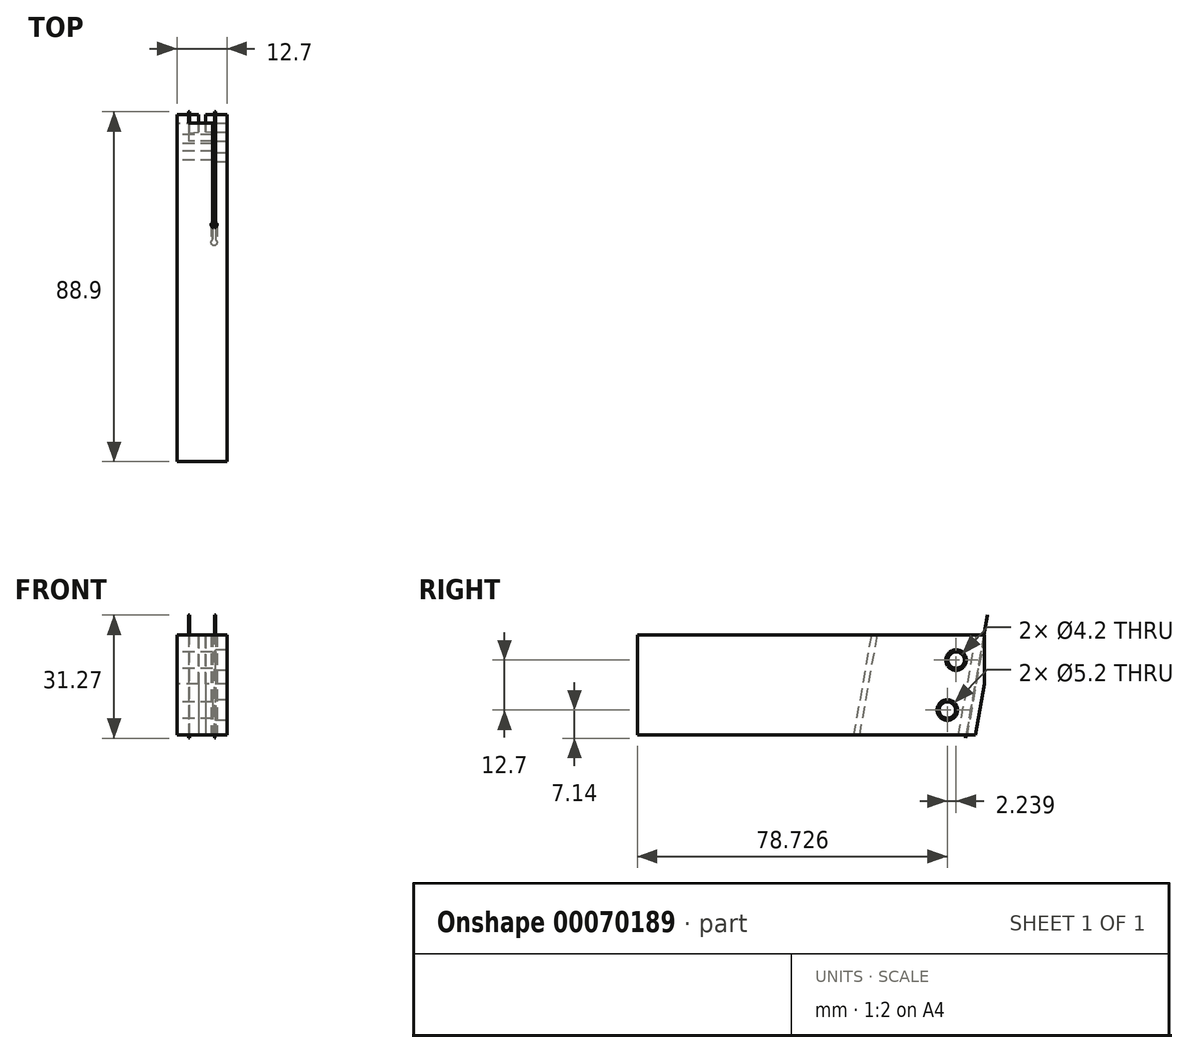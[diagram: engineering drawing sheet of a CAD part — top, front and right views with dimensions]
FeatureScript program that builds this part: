
annotation { "Feature Type Name" : "Feature", "Feature Type Description" : "" }
export const myFeature = defineFeature(function(context is Context, id is Id, definition is map)
    precondition{}
    {
        {
            var Q0;
            Q0=qCreatedBy(makeId("Right.planeOp"),FACE);
            var sketch = newSketch(context, id + "F0", { "sketchPlane" : qUnion([Q0])});
            skLineSegment(sketch, "E0", {"start": v(12.7, 0) * mm, "end": v(7.19, -31.27) * mm});
            skLineSegment(sketch, "E1", {"start": v(7.19, -31.27) * mm, "end": v(5.2, -30.92) * mm});
            skLineSegment(sketch, "E2", {"start": v(5.2, -30.92) * mm, "end": v(9.75, -5.11) * mm});
            skLineSegment(sketch, "E3", {"start": v(9.75, -5.11) * mm, "end": v(12.7, 0) * mm});
            skLineSegment(sketch, "E4", {"start": v(11.94, -17.49) * mm, "end": v(9.65, -30.48) * mm});
            skLineSegment(sketch, "E5", {"start": v(9.65, -30.48) * mm, "end": v(-76.2, -30.48) * mm});
            skLineSegment(sketch, "E6", {"start": v(-76.2, -30.48) * mm, "end": v(-76.2, -5.08) * mm});
            skLineSegment(sketch, "E7", {"start": v(-76.2, -5.08) * mm, "end": v(11.94, -5.08) * mm});
            skLineSegment(sketch, "E8", {"start": v(11.94, -5.08) * mm, "end": v(11.94, -17.49) * mm});
            skLineSegment(sketch, "E9", {"start": v(5.89, -5.08) * mm, "end": v(1.4, -30.48) * mm, "construction": true});
            skPoint(sketch, "E10", {"position": v(4.77, -11.43) * mm});
            skPoint(sketch, "E11", {"position": v(2.53, -24.13) * mm});
            skCircle(sketch, "E12", {"center": v(4.77, -11.43) * mm, "radius": 2.1 * mm});
            skCircle(sketch, "E13", {"center": v(4.77, -11.43) * mm, "radius": 2.6 * mm});
            skCircle(sketch, "E14", {"center": v(2.53, -24.13) * mm, "radius": 2.6 * mm});
            skCircle(sketch, "E15", {"center": v(2.53, -24.13) * mm, "radius": 2.1 * mm});
            skSolve(sketch);
        }
        {
            var Q0;
            {var subQ0=sQuery(id+"F0.wireOp",EDGE,"E3");Q0=makeQuery(id+"F0.imprint","IMPRINT",FACE,{"disambiguationData":[TD([[makeQuery(id+"F0.imprint","IMPRINT",EDGE,{"derivedFrom":subQ0}),-1.0]])]});}
            var Q1;
            {var subQ0=sQuery(id+"F0.wireOp",EDGE,"E1");Q1=makeQuery(id+"F0.imprint","IMPRINT",FACE,{"disambiguationData":[TD([[makeQuery(id+"F0.imprint","IMPRINT",EDGE,{"derivedFrom":subQ0}),-1.0]])]});}
            var Q2;
            {var subQ1=sQuery(id+"F0.wireOp",EDGE,"E0");var subQ7=sQuery(id+"F0.wireOp",EDGE,"E7");var subQ9=makeQuery(id+"F0.imprint","INTERSECT",VERTEX,{"derivedFrom":[subQ1,subQ7]});Q2=makeQuery(id+"F0.imprint","IMPRINT",FACE,{"disambiguationData":[TD([[makeQuery(id+"F0.imprint","IMPRINT",EDGE,{"disambiguationData":[TD([[subQ9,-1.0]])],"derivedFrom":subQ1}),-1.0]])]});}
            extrude(context, id + "F1", {"entities" : qUnion([Q0, Q1, Q2]), "depth" : 6.9 * mm});
        }
        {
            var Q0;
            {var subQ5=sQuery(id+"F0.wireOp",EDGE,"E4");Q0=makeQuery(id+"F0.imprint","IMPRINT",FACE,{"disambiguationData":[TD([[makeQuery(id+"F0.imprint","IMPRINT",EDGE,{"derivedFrom":subQ5}),-1.0]])]});}
            var Q1;
            {var subQ1=sQuery(id+"F0.wireOp",EDGE,"E0");var subQ7=sQuery(id+"F0.wireOp",EDGE,"E7");var subQ9=makeQuery(id+"F0.imprint","INTERSECT",VERTEX,{"derivedFrom":[subQ1,subQ7]});Q1=makeQuery(id+"F0.imprint","IMPRINT",FACE,{"disambiguationData":[TD([[makeQuery(id+"F0.imprint","IMPRINT",EDGE,{"disambiguationData":[TD([[subQ9,-1.0]])],"derivedFrom":subQ1}),-1.0]])]});}
            var Q2;
            {var subQ0=sQuery(id+"F0.wireOp",EDGE,"E6");Q2=makeQuery(id+"F0.imprint","IMPRINT",FACE,{"disambiguationData":[TD([[makeQuery(id+"F0.imprint","IMPRINT",EDGE,{"derivedFrom":subQ0}),-1.0]])]});}
            var Q3;
            Q3=makeQuery(id+"F0.imprint","IMPRINT",FACE,{"disambiguationData":[TD([[makeQuery(id+"F0.imprint","IMPRINT",EDGE,{"derivedFrom":sQuery(id+"F0.wireOp",EDGE,"E14")}),1.0]])]});
            var Q4;
            Q4=makeQuery(id+"F0.imprint","IMPRINT",FACE,{"disambiguationData":[TD([[makeQuery(id+"F0.imprint","IMPRINT",EDGE,{"derivedFrom":sQuery(id+"F0.wireOp",EDGE,"E12")}),-1.0]])]});
            extrude(context, id + "F2", {"entities" : qUnion([Q0, Q1, Q2, Q3, Q4]), "depth" : 9.8 * mm, "hasSecondDirection" : true, "secondDirectionOppositeDirection" : true, "secondDirectionDepth" : 2.9 * mm});
        }
        {
            var Q0;
            Q0=makeQuery(id+"F1.opExtrude","SWEPT_FACE",FACE,{"disambiguationData":[OSD([sQuery(id+"F0.wireOp",EDGE,"E1")])]});
            var sketch = newSketch(context, id + "F3", { "sketchPlane" : qUnion([Q0])});
            skLineSegment(sketch, "E16.0.0", {"start": v(0, -10.49) * mm, "end": v(0, -12.5) * mm});
            skLineSegment(sketch, "E16.0.1", {"start": v(0, -12.5) * mm, "end": v(6.9, -12.5) * mm, "construction": true});
            skLineSegment(sketch, "E16.0.2", {"start": v(6.9, -12.5) * mm, "end": v(6.9, -10.49) * mm});
            skLineSegment(sketch, "E16.0.3", {"start": v(6.9, -10.49) * mm, "end": v(0, -10.49) * mm, "construction": true});
            skLineSegment(sketch, "E17.0.0", {"start": v(-2.9, 69.75) * mm, "end": v(-2.9, -14.8) * mm, "construction": true});
            skLineSegment(sketch, "E17.0.1", {"start": v(-2.9, -14.8) * mm, "end": v(9.8, -14.8) * mm, "construction": true});
            skLineSegment(sketch, "E17.0.2", {"start": v(9.8, -14.8) * mm, "end": v(9.8, 69.75) * mm, "construction": true});
            skLineSegment(sketch, "E17.0.3", {"start": v(9.8, 69.75) * mm, "end": v(-2.9, 69.75) * mm, "construction": true});
            skLineSegment(sketch, "E18", {"start": v(0, -12.48) * mm, "end": v(2.54, -12.7) * mm});
            skLineSegment(sketch, "E19", {"start": v(2.54, -12.7) * mm, "end": v(2.54, -14.8) * mm});
            skLineSegment(sketch, "E20", {"start": v(6.9, -12.48) * mm, "end": v(4.37, -12.7) * mm});
            skLineSegment(sketch, "E21", {"start": v(4.37, -12.7) * mm, "end": v(4.37, -14.8) * mm});
            skLineSegment(sketch, "E22", {"start": v(6.9, -10.49) * mm, "end": v(6.9, 14.25) * mm});
            skArc(sketch, "E23", {"start": v(6.9, 14.25) * mm, "mid": v(6.53, 15.67) * mm, "end": v(6.15, 14.25) * mm});
            skLineSegment(sketch, "E24", {"start": v(6.15, 14.25) * mm, "end": v(6.15, -10.49) * mm});
            skLineSegment(sketch, "E25", {"start": v(0, -10.49) * mm, "end": v(6.15, -10.49) * mm, "construction": true});
            skLineSegment(sketch, "E26", {"start": v(2.54, -14.8) * mm, "end": v(4.37, -14.8) * mm});
            skLineSegment(sketch, "E27", {"start": v(6.9, 14.25) * mm, "end": v(6.53, 14.91) * mm, "construction": true});
            skLineSegment(sketch, "E28", {"start": v(6.15, 14.25) * mm, "end": v(6.53, 14.91) * mm, "construction": true});
            skSolve(sketch);
        }
        {
            var Q0;
            {var subQ8=sQuery(id+"F3.wireOp",EDGE,"E18");var subQ9=sQuery(id+"F3.wireOp",EDGE,"E16.0.0");var subQ10=makeQuery(id+"F3.imprint","INTERSECT",VERTEX,{"derivedFrom":[subQ9,subQ8]});Q0=makeQuery(id+"F3.imprint","IMPRINT",FACE,{"disambiguationData":[TD([[makeQuery(id+"F3.imprint","IMPRINT",EDGE,{"disambiguationData":[TD([[subQ10,-1.0]])],"derivedFrom":subQ9}),-1.0]])]});}
            var Q1;
            {var subQ4=sQuery(id+"F3.wireOp",EDGE,"E19");Q1=makeQuery(id+"F3.imprint","IMPRINT",FACE,{"disambiguationData":[TD([[makeQuery(id+"F3.imprint","IMPRINT",EDGE,{"derivedFrom":subQ4}),1.0]])]});}
            var Q2;
            {var subQ0=sQuery(id+"F3.wireOp",EDGE,"E22");Q2=makeQuery(id+"F3.imprint","IMPRINT",FACE,{"disambiguationData":[TD([[makeQuery(id+"F3.imprint","IMPRINT",EDGE,{"derivedFrom":subQ0}),1.0]])]});}
            extrude(context, id + "F4", {"entities" : qUnion([Q0, Q1, Q2]), "operationType" : NewBodyOperationType.REMOVE, "endBound" : BoundingType.THROUGH_ALL, "oppositeDirection" : true, "depth" : 25.4 * mm, "hasSecondDirection" : true, "secondDirectionBound" : SecondDirectionBoundingType.THROUGH_ALL, "secondDirectionOppositeDirection" : false, "secondDirectionDepth" : 25.4 * mm});
        }
        {
            var Q0;
            Q0=makeQuery(id+"F4.boolean.opBoolean","COPY",FACE,{"derivedFrom":makeQuery(id+"F4.opExtrude","SWEPT_FACE",FACE,{"disambiguationData":[OSD([sQuery(id+"F3.wireOp",EDGE,"E24")])]})});
            var sketch = newSketch(context, id + "F5", { "sketchPlane" : qUnion([Q0])});
            skCircle(sketch, "E29.0", {"center": v(4.77, -11.43) * mm, "radius": 2.6 * mm});
            skCircle(sketch, "E30.0", {"center": v(2.53, -24.13) * mm, "radius": 2.6 * mm});
            skSolve(sketch);
        }
        {
            var Q0;
            Q0=makeQuery(id+"F5.imprint","IMPRINT",FACE,{"disambiguationData":[TD([[makeQuery(id+"F5.imprint","IMPRINT",EDGE,{"derivedFrom":sQuery(id+"F5.wireOp",EDGE,"E29.0")}),1.0]])]});
            var Q1;
            Q1=makeQuery(id+"F5.imprint","IMPRINT",FACE,{"disambiguationData":[TD([[makeQuery(id+"F5.imprint","IMPRINT",EDGE,{"derivedFrom":sQuery(id+"F5.wireOp",EDGE,"E30.0")}),1.0]])]});
            var Q2;
            Q2=makeQuery(id+"F2.opExtrude","CAP_FACE",FACE,{"disambiguationData":[OSD([sQuery(id+"F0.wireOp",EDGE,"E4"),sQuery(id+"F0.wireOp",EDGE,"E5"),sQuery(id+"F0.wireOp",EDGE,"E6"),sQuery(id+"F0.wireOp",EDGE,"E7"),sQuery(id+"F0.wireOp",EDGE,"E8"),sQuery(id+"F0.wireOp",EDGE,"E12"),sQuery(id+"F0.wireOp",EDGE,"E15")])],"isStart":false});
            extrude(context, id + "F6", {"entities" : qUnion([Q0, Q1]), "operationType" : NewBodyOperationType.REMOVE, "endBound" : BoundingType.UP_TO_SURFACE, "endBoundEntityFace" : qUnion([Q2]), "depth" : 25.4 * mm});
        }
    });
